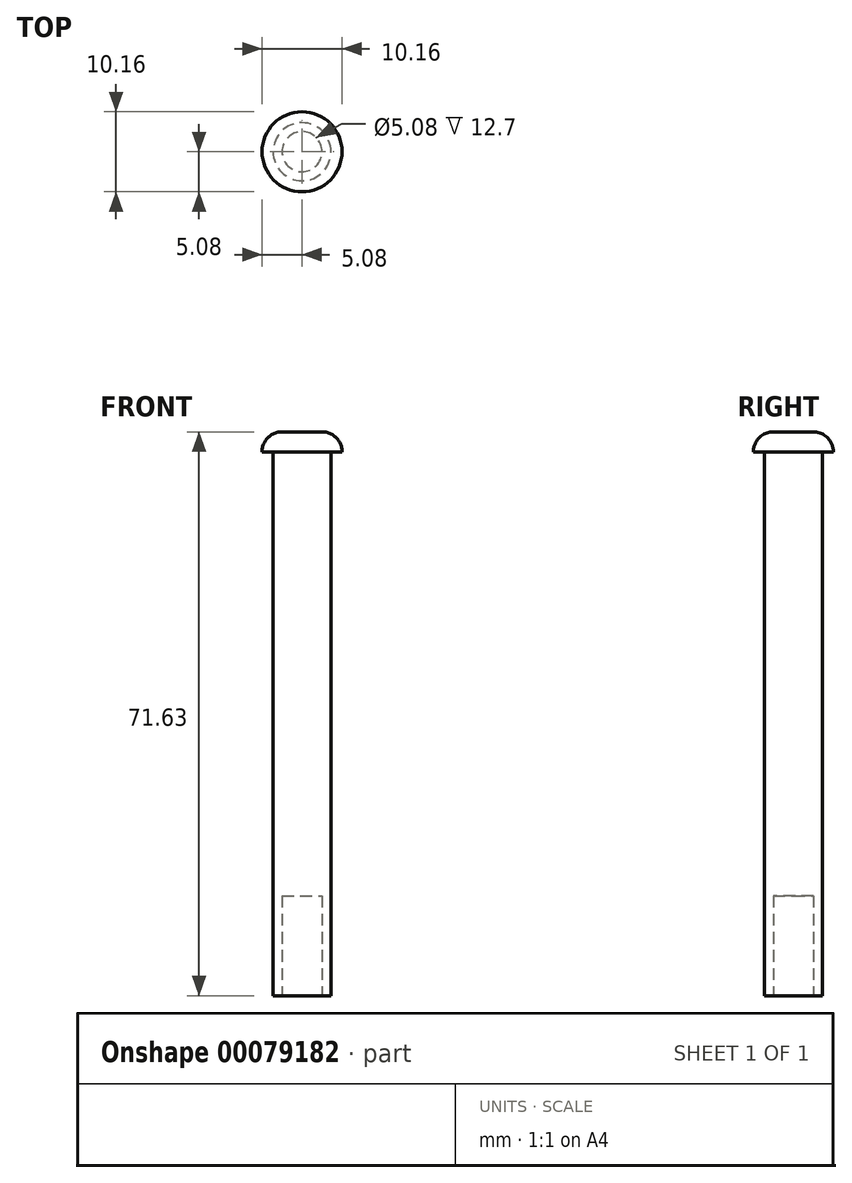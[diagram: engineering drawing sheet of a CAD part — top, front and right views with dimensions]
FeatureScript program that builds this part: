
annotation { "Feature Type Name" : "Feature", "Feature Type Description" : "" }
export const myFeature = defineFeature(function(context is Context, id is Id, definition is map)
    precondition{}
    {
        {
            var Q0;
            Q0=qCreatedBy(makeId("Top.planeOp"),FACE);
            var sketch = newSketch(context, id + "F0", { "sketchPlane" : qUnion([Q0])});
            skCircle(sketch, "E0", {"center": v(0, 0) * mm, "radius": 3.68 * mm});
            skSolve(sketch);
        }
        {
            var Q0;
            Q0=qSketchRegion(id+"F0",true);
            extrude(context, id + "F1", {"entities" : qUnion([Q0]), "depth" : 69.1 * mm});
        }
        {
            var Q0;
            Q0=makeQuery(id+"F1.opExtrude","CAP_FACE",FACE,{"disambiguationData":[OSD([sQuery(id+"F0.wireOp",EDGE,"E0")])],"isStart":false});
            var sketch = newSketch(context, id + "F2", { "sketchPlane" : qUnion([Q0])});
            skCircle(sketch, "E1", {"center": v(0, 0) * mm, "radius": 5.08 * mm});
            skSolve(sketch);
        }
        {
            var Q0;
            Q0=qSketchRegion(id+"F2",true);
            extrude(context, id + "F3", {"entities" : qUnion([Q0]), "operationType" : NewBodyOperationType.ADD, "depth" : 2.54 * mm});
        }
        {
            var Q0;
            Q0=makeQuery(id+"F3.opExtrude","CAP_EDGE",EDGE,{"disambiguationData":[OSD([sQuery(id+"F2.wireOp",EDGE,"E1")])],"isStart":false});
            fillet(context, id + "F4", {"entities" : qUnion([Q0]), "radius" : 2.54 * mm, "tangentPropagation" : true, "allowEdgeOverflow" : false});
        }
        {
            var Q0;
            Q0=makeQuery(id+"F1.opExtrude","CAP_FACE",FACE,{"disambiguationData":[OSD([sQuery(id+"F0.wireOp",EDGE,"E0")])],"isStart":true});
            var sketch = newSketch(context, id + "F5", { "sketchPlane" : qUnion([Q0])});
            skCircle(sketch, "E2", {"center": v(0, 0) * mm, "radius": 2.54 * mm});
            skSolve(sketch);
        }
        {
            var Q0;
            Q0=qSketchRegion(id+"F5",true);
            extrude(context, id + "F6", {"entities" : qUnion([Q0]), "operationType" : NewBodyOperationType.REMOVE, "oppositeDirection" : true, "depth" : 12.7 * mm});
        }
    });
